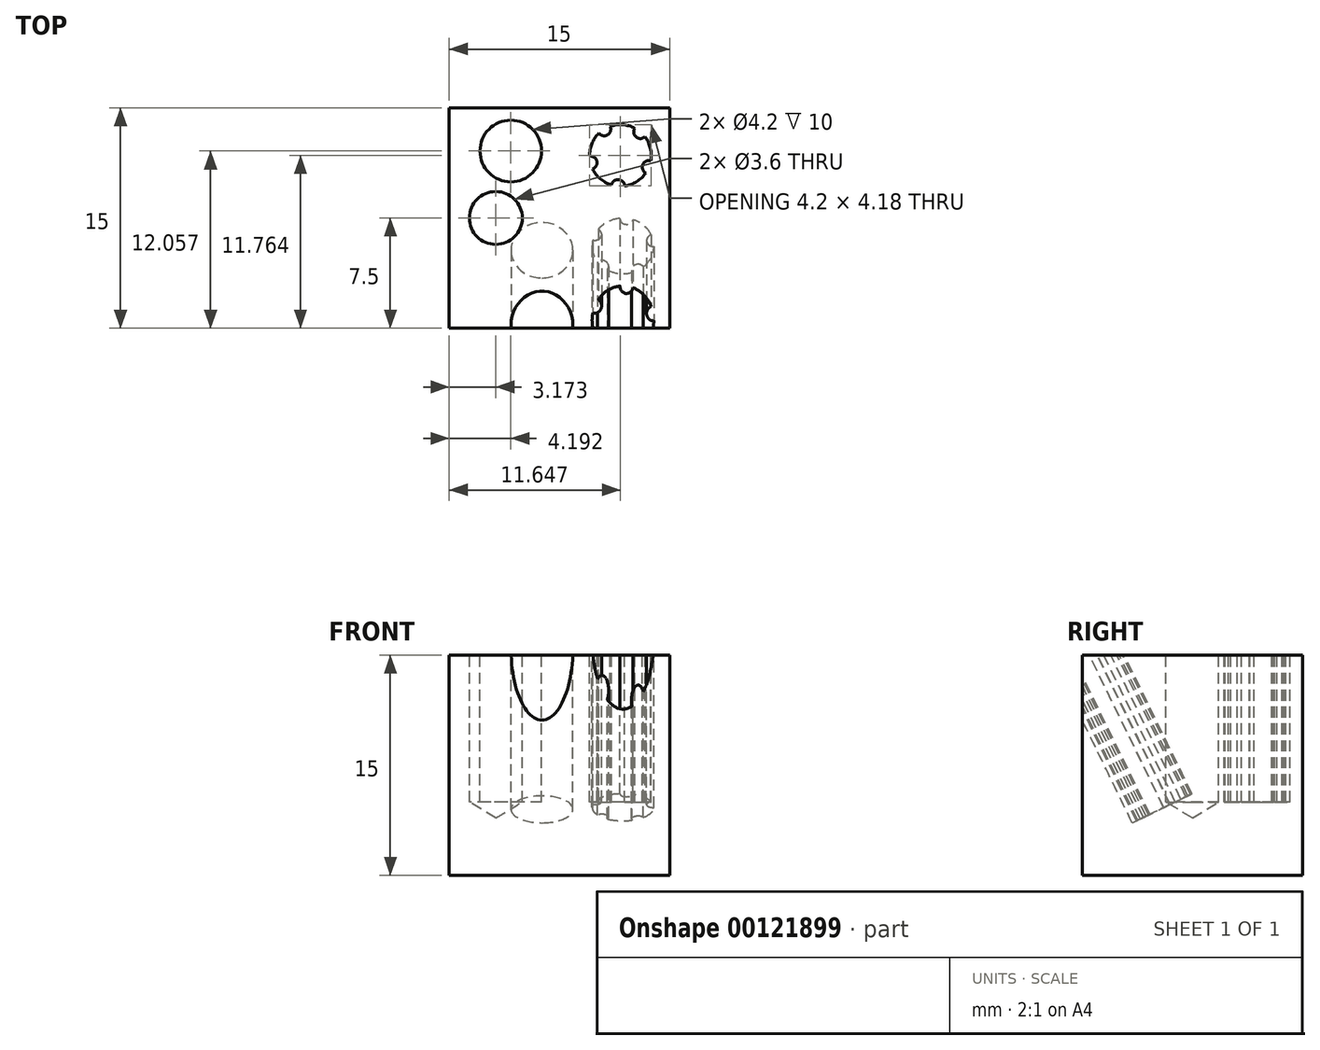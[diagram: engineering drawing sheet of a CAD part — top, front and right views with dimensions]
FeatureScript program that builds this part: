
annotation { "Feature Type Name" : "Feature", "Feature Type Description" : "" }
export const myFeature = defineFeature(function(context is Context, id is Id, definition is map)
    precondition{}
    {
        {
            var Q0;
            Q0=qCreatedBy(makeId("Top.planeOp"),FACE);
            var sketch = newSketch(context, id + "F0", { "sketchPlane" : qUnion([Q0])});
            skLineSegment(sketch, "E0.bottom", {"start": v(7.5, -7.5) * mm, "end": v(-7.5, -7.5) * mm});
            skLineSegment(sketch, "E0.top", {"start": v(7.5, 7.5) * mm, "end": v(-7.5, 7.5) * mm});
            skLineSegment(sketch, "E0.left", {"start": v(7.5, -7.5) * mm, "end": v(7.5, 7.5) * mm});
            skLineSegment(sketch, "E0.right", {"start": v(-7.5, -7.5) * mm, "end": v(-7.5, 7.5) * mm});
            skPoint(sketch, "E0.middle", {"position": v(0, 0) * mm});
            skSolve(sketch);
        }
        {
            var Q0;
            Q0=makeQuery(id+"F0.imprint","IMPRINT",FACE,{"disambiguationData":[TD([[makeQuery(id+"F0.imprint","IMPRINT",EDGE,{"derivedFrom":sQuery(id+"F0.wireOp",EDGE,"E0.bottom")}),-1.0]])]});
            extrude(context, id + "F1", {"entities" : qUnion([Q0]), "depth" : 15 * mm});
        }
        {
            var Q0;
            Q0=makeQuery(id+"F1.opExtrude","CAP_FACE",FACE,{"disambiguationData":[OSD([sQuery(id+"F0.wireOp",EDGE,"E0.bottom"),sQuery(id+"F0.wireOp",EDGE,"E0.top"),sQuery(id+"F0.wireOp",EDGE,"E0.left"),sQuery(id+"F0.wireOp",EDGE,"E0.right")])],"isStart":false});
            var sketch = newSketch(context, id + "F2", { "sketchPlane" : qUnion([Q0])});
            skCircle(sketch, "E1", {"center": v(-3.3, 4.56) * mm, "radius": 2.1 * mm});
            skCircle(sketch, "E2", {"center": v(4.15, 4.25) * mm, "radius": 1.65 * mm});
            skArc(sketch, "E3", {"start": v(3.45, 6.24) * mm, "mid": v(2.8, 6.42) * mm, "end": v(2.69, 5.77) * mm, "construction": true});
            skArc(sketch, "E4", {"start": v(2.69, 5.77) * mm, "mid": v(3.28, 5.66) * mm, "end": v(3.45, 6.24) * mm});
            skArc(sketch, "E5", {"start": v(3.45, 6.24) * mm, "mid": v(3.04, 6.04) * mm, "end": v(2.69, 5.77) * mm, "construction": true});
            skArc(sketch, "E6", {"start": v(2.69, 5.77) * mm, "mid": v(2.2, 5.05) * mm, "end": v(2.05, 4.2) * mm});
            skArc(sketch, "E7.1.0", {"start": v(2.26, 3.33) * mm, "mid": v(2.54, 3.86) * mm, "end": v(2.05, 4.2) * mm});
            skArc(sketch, "E7.2.0", {"start": v(4.44, 2.17) * mm, "mid": v(4.02, 2.6) * mm, "end": v(3.55, 2.24) * mm});
            skArc(sketch, "E7.3.0", {"start": v(6.21, 3.89) * mm, "mid": v(5.67, 3.63) * mm, "end": v(5.87, 3.06) * mm});
            skArc(sketch, "E7.4.0", {"start": v(5.13, 6.1) * mm, "mid": v(5.22, 5.51) * mm, "end": v(5.82, 5.53) * mm});
            skArc(sketch, "E8", {"start": v(5.13, 6.1) * mm, "mid": v(4.3, 6.35) * mm, "end": v(3.45, 6.24) * mm});
            skArc(sketch, "E9", {"start": v(5.82, 5.53) * mm, "mid": v(5.5, 5.85) * mm, "end": v(5.13, 6.1) * mm, "construction": true});
            skArc(sketch, "E10", {"start": v(6.21, 3.89) * mm, "mid": v(6.19, 4.75) * mm, "end": v(5.82, 5.53) * mm});
            skArc(sketch, "E11", {"start": v(5.87, 3.06) * mm, "mid": v(6.09, 3.46) * mm, "end": v(6.21, 3.89) * mm, "construction": true});
            skArc(sketch, "E12", {"start": v(4.44, 2.17) * mm, "mid": v(5.25, 2.47) * mm, "end": v(5.87, 3.06) * mm});
            skArc(sketch, "E13", {"start": v(3.55, 2.24) * mm, "mid": v(3.99, 2.16) * mm, "end": v(4.44, 2.17) * mm, "construction": true});
            skArc(sketch, "E14", {"start": v(2.26, 3.33) * mm, "mid": v(2.79, 2.65) * mm, "end": v(3.55, 2.24) * mm});
            skArc(sketch, "E15", {"start": v(2.05, 4.2) * mm, "mid": v(2.1, 3.76) * mm, "end": v(2.26, 3.33) * mm, "construction": true});
            skSolve(sketch);
        }
        {
            var Q0;
            Q0=makeQuery(id+"F2.imprint","IMPRINT",FACE,{"disambiguationData":[TD([[makeQuery(id+"F2.imprint","IMPRINT",EDGE,{"derivedFrom":sQuery(id+"F2.wireOp",EDGE,"E1")}),1.0]])]});
            var Q1;
            Q1=sQuery(id+"F2.wireOp",EDGE,"E15");
            var Q2;
            Q2=sQuery(id+"F2.wireOp",EDGE,"E13");
            var Q3;
            Q3=sQuery(id+"F2.wireOp",EDGE,"E11");
            var Q4;
            Q4=sQuery(id+"F2.wireOp",EDGE,"E9");
            extrude(context, id + "F3", {"entities" : qUnion([Q0]), "operationType" : NewBodyOperationType.REMOVE, "surfaceEntities" : qUnion([Q1, Q2, Q3, Q4]), "oppositeDirection" : true, "depth" : 10 * mm});
        }
        {
            var Q0;
            {var subQ5=sQuery(id+"F2.wireOp",EDGE,"E8");Q0=makeQuery(id+"F2.imprint","IMPRINT",FACE,{"disambiguationData":[TD([[makeQuery(id+"F2.imprint","IMPRINT",EDGE,{"derivedFrom":subQ5}),1.0]])]});}
            var Q1;
            {var subQ5=sQuery(id+"F2.wireOp",EDGE,"E14");Q1=makeQuery(id+"F2.imprint","IMPRINT",FACE,{"disambiguationData":[TD([[makeQuery(id+"F2.imprint","IMPRINT",EDGE,{"derivedFrom":subQ5}),1.0]])]});}
            var Q2;
            {var subQ5=sQuery(id+"F2.wireOp",EDGE,"E12");Q2=makeQuery(id+"F2.imprint","IMPRINT",FACE,{"disambiguationData":[TD([[makeQuery(id+"F2.imprint","IMPRINT",EDGE,{"derivedFrom":subQ5}),1.0]])]});}
            var Q3;
            {var subQ5=sQuery(id+"F2.wireOp",EDGE,"E10");Q3=makeQuery(id+"F2.imprint","IMPRINT",FACE,{"disambiguationData":[TD([[makeQuery(id+"F2.imprint","IMPRINT",EDGE,{"derivedFrom":subQ5}),1.0]])]});}
            var Q4;
            {var subQ5=sQuery(id+"F2.wireOp",EDGE,"E6");Q4=makeQuery(id+"F2.imprint","IMPRINT",FACE,{"disambiguationData":[TD([[makeQuery(id+"F2.imprint","IMPRINT",EDGE,{"derivedFrom":subQ5}),1.0]])]});}
            var Q5;
            {var subQ0=sQuery(id+"F2.wireOp",EDGE,"E2");var subQ4=makeQuery(id+"F2.imprint","INTERSECT",VERTEX,{"derivedFrom":[subQ0,sQuery(id+"F2.wireOp",EDGE,"E7.1.0")]});Q5=makeQuery(id+"F2.imprint","IMPRINT",FACE,{"disambiguationData":[TD([[makeQuery(id+"F2.imprint","IMPRINT",EDGE,{"disambiguationData":[TD([[subQ4,1.0]])],"derivedFrom":subQ0}),1.0]])]});}
            extrude(context, id + "F4", {"entities" : qUnion([Q0, Q1, Q2, Q3, Q4, Q5]), "operationType" : NewBodyOperationType.REMOVE, "oppositeDirection" : true, "depth" : 10 * mm});
        }
        {
            var Q0;
            Q0=makeQuery(id+"F2.imprint","IMPRINT",FACE,{"disambiguationData":[TD([[makeQuery(id+"F2.imprint","IMPRINT",EDGE,{"derivedFrom":sQuery(id+"F2.wireOp",EDGE,"E1")}),-1.0]])]});
            var sketch = newSketch(context, id + "F5", { "sketchPlane" : qUnion([Q0])});
            skPoint(sketch, "E16", {"position": v(-4.33, 0) * mm});
            skSolve(sketch);
        }
        {
            var Q0;
            Q0=sQuery(id+"F5.wireOp",VERTEX,"E16");
            var Q1;
            Q1=makeQuery(id+"F1.opExtrude","SWEPT_BODY",BODY,{"disambiguationData":[OSD([sQuery(id+"F0.wireOp",EDGE,"E0.bottom"),sQuery(id+"F0.wireOp",EDGE,"E0.top"),sQuery(id+"F0.wireOp",EDGE,"E0.left"),sQuery(id+"F0.wireOp",EDGE,"E0.right")])]});
            hole(context, id + "F6", {"style" : HoleStyle.SIMPLE, "endStyle" : HoleEndStyle.BLIND, "holeDiameter" : 3.6 * mm, "holeDepth" : 10 * mm, "startFromSketch" : true, "locations" : qUnion([Q0]), "scope" : qUnion([Q1])});
        }
        {
            var Q0;
            Q0=makeQuery(id+"F2.imprint","IMPRINT",FACE,{"disambiguationData":[TD([[makeQuery(id+"F2.imprint","IMPRINT",EDGE,{"derivedFrom":sQuery(id+"F2.wireOp",EDGE,"E1")}),-1.0]])]});
            var sketch = newSketch(context, id + "F7", { "sketchPlane" : qUnion([Q0])});
            skLineSegment(sketch, "E17.0", {"start": v(7.5, -7.5) * mm, "end": v(-7.5, -7.5) * mm});
            skLineSegment(sketch, "E18.0", {"start": v(-7.5, -7.5) * mm, "end": v(-7.5, 7.5) * mm});
            skLineSegment(sketch, "E19.0", {"start": v(7.5, -7.5) * mm, "end": v(7.5, 7.5) * mm});
            skLineSegment(sketch, "E20", {"start": v(-7.5, -3.49) * mm, "end": v(7.5, -3.49) * mm});
            skSolve(sketch);
        }
        {
            var Q0;
            Q0=sQuery(id+"F7.wireOp",EDGE,"E20");
            cPlane(context, id + "F8", {"entities" : qUnion([Q0]), "cplaneType" : CPlaneType.LINE_ANGLE, "offset" : 25 * mm, "angle" : (180 - (90 - 26)) * degree, "width" : 150 * mm, "height" : 150 * mm});
        }
        {
            var Q0;
            Q0=qCreatedBy(id+"F8.planeOp",FACE);
            var sketch = newSketch(context, id + "F9", { "sketchPlane" : qUnion([Q0])});
            skCircle(sketch, "E21", {"center": v(-1.19, 0) * mm, "radius": 2.1 * mm});
            skCircle(sketch, "E22", {"center": v(4.32, 0.32) * mm, "radius": 1.65 * mm});
            skArc(sketch, "E23", {"start": v(5, 2.3) * mm, "mid": v(4.62, 2.85) * mm, "end": v(4.12, 2.41) * mm, "construction": true});
            skArc(sketch, "E24", {"start": v(4.12, 2.41) * mm, "mid": v(4.52, 1.96) * mm, "end": v(5, 2.3) * mm});
            skArc(sketch, "E25", {"start": v(5, 2.3) * mm, "mid": v(4.57, 2.4) * mm, "end": v(4.12, 2.41) * mm, "construction": true});
            skArc(sketch, "E26", {"start": v(4.12, 2.41) * mm, "mid": v(3.3, 2.15) * mm, "end": v(2.65, 1.59) * mm});
            skArc(sketch, "E27.1.0", {"start": v(2.27, 0.78) * mm, "mid": v(2.82, 1.01) * mm, "end": v(2.65, 1.59) * mm});
            skArc(sketch, "E27.2.0", {"start": v(3.26, -1.49) * mm, "mid": v(3.2, -0.89) * mm, "end": v(2.6, -0.88) * mm});
            skArc(sketch, "E27.3.0", {"start": v(5.71, -1.25) * mm, "mid": v(5.13, -1.12) * mm, "end": v(4.93, -1.69) * mm});
            skArc(sketch, "E27.4.0", {"start": v(6.25, 1.16) * mm, "mid": v(5.94, 0.64) * mm, "end": v(6.42, 0.28) * mm});
            skArc(sketch, "E28", {"start": v(6.25, 1.16) * mm, "mid": v(5.75, 1.86) * mm, "end": v(5, 2.3) * mm});
            skArc(sketch, "E29", {"start": v(6.42, 0.28) * mm, "mid": v(6.38, 0.73) * mm, "end": v(6.25, 1.16) * mm, "construction": true});
            skArc(sketch, "E30", {"start": v(5.71, -1.25) * mm, "mid": v(6.23, -0.56) * mm, "end": v(6.42, 0.28) * mm});
            skArc(sketch, "E31", {"start": v(4.93, -1.69) * mm, "mid": v(5.35, -1.51) * mm, "end": v(5.71, -1.25) * mm, "construction": true});
            skArc(sketch, "E32", {"start": v(3.26, -1.49) * mm, "mid": v(4.07, -1.76) * mm, "end": v(4.93, -1.69) * mm});
            skArc(sketch, "E33", {"start": v(2.6, -0.88) * mm, "mid": v(2.9, -1.22) * mm, "end": v(3.26, -1.49) * mm, "construction": true});
            skArc(sketch, "E34", {"start": v(2.27, 0.78) * mm, "mid": v(2.26, -0.09) * mm, "end": v(2.6, -0.88) * mm});
            skArc(sketch, "E35", {"start": v(2.65, 1.59) * mm, "mid": v(2.42, 1.2) * mm, "end": v(2.27, 0.78) * mm, "construction": true});
            skSolve(sketch);
        }
        {
            var Q0;
            Q0=makeQuery(id+"F9.imprint","IMPRINT",FACE,{"disambiguationData":[TD([[makeQuery(id+"F9.imprint","IMPRINT",EDGE,{"derivedFrom":sQuery(id+"F9.wireOp",EDGE,"E21")}),1.0]])]});
            extrude(context, id + "F10", {"entities" : qUnion([Q0]), "operationType" : NewBodyOperationType.REMOVE, "oppositeDirection" : true, "depth" : 10 * mm, "hasSecondDirection" : true, "secondDirectionOppositeDirection" : false, "secondDirectionDepth" : 10 * mm});
        }
        {
            var Q0;
            {var subQ5=sQuery(id+"F9.wireOp",EDGE,"E32");Q0=makeQuery(id+"F9.imprint","IMPRINT",FACE,{"disambiguationData":[TD([[makeQuery(id+"F9.imprint","IMPRINT",EDGE,{"derivedFrom":subQ5}),1.0]])]});}
            var Q1;
            {var subQ5=sQuery(id+"F9.wireOp",EDGE,"E34");Q1=makeQuery(id+"F9.imprint","IMPRINT",FACE,{"disambiguationData":[TD([[makeQuery(id+"F9.imprint","IMPRINT",EDGE,{"derivedFrom":subQ5}),1.0]])]});}
            var Q2;
            {var subQ0=sQuery(id+"F9.wireOp",EDGE,"E22");var subQ3=makeQuery(id+"F9.imprint","INTERSECT",VERTEX,{"derivedFrom":[subQ0,sQuery(id+"F9.wireOp",EDGE,"E24")]});Q2=makeQuery(id+"F9.imprint","IMPRINT",FACE,{"disambiguationData":[TD([[makeQuery(id+"F9.imprint","IMPRINT",EDGE,{"disambiguationData":[TD([[subQ3,1.0]])],"derivedFrom":subQ0}),1.0]])]});}
            var Q3;
            {var subQ5=sQuery(id+"F9.wireOp",EDGE,"E30");Q3=makeQuery(id+"F9.imprint","IMPRINT",FACE,{"disambiguationData":[TD([[makeQuery(id+"F9.imprint","IMPRINT",EDGE,{"derivedFrom":subQ5}),1.0]])]});}
            var Q4;
            {var subQ5=sQuery(id+"F9.wireOp",EDGE,"E28");Q4=makeQuery(id+"F9.imprint","IMPRINT",FACE,{"disambiguationData":[TD([[makeQuery(id+"F9.imprint","IMPRINT",EDGE,{"derivedFrom":subQ5}),1.0]])]});}
            var Q5;
            {var subQ5=sQuery(id+"F9.wireOp",EDGE,"E26");Q5=makeQuery(id+"F9.imprint","IMPRINT",FACE,{"disambiguationData":[TD([[makeQuery(id+"F9.imprint","IMPRINT",EDGE,{"derivedFrom":subQ5}),1.0]])]});}
            extrude(context, id + "F11", {"entities" : qUnion([Q0, Q1, Q2, Q3, Q4, Q5]), "operationType" : NewBodyOperationType.REMOVE, "oppositeDirection" : true, "depth" : 10 * mm, "hasSecondDirection" : true, "secondDirectionOppositeDirection" : false, "secondDirectionDepth" : 10 * mm});
        }
    });
